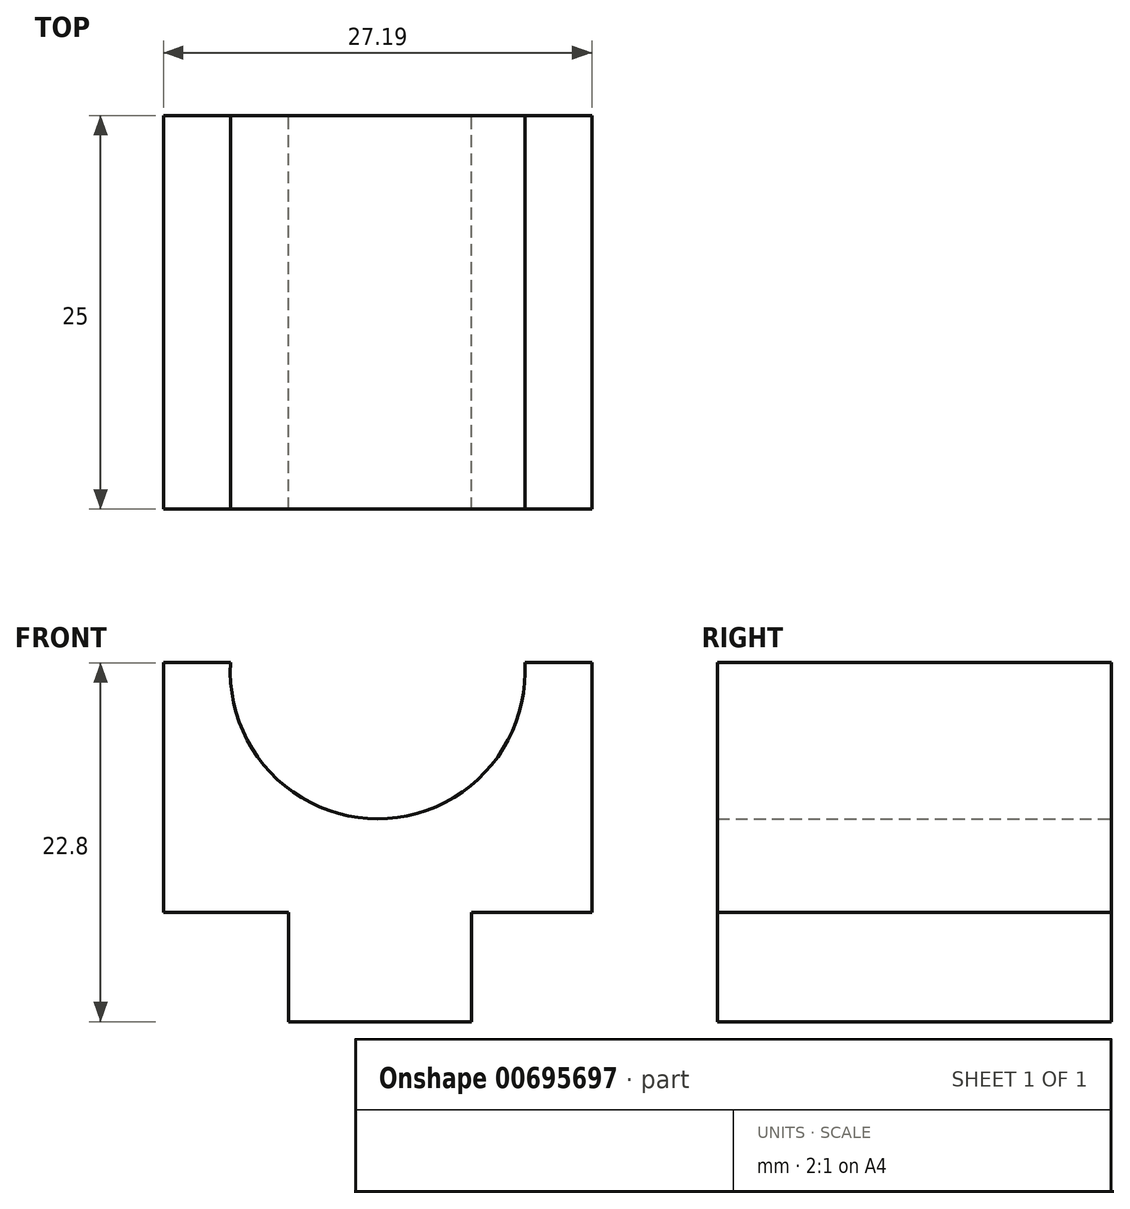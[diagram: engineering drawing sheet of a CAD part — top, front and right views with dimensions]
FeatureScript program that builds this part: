
annotation { "Feature Type Name" : "Feature", "Feature Type Description" : "" }
export const myFeature = defineFeature(function(context is Context, id is Id, definition is map)
    precondition{}
    {
        {
            var Q0;
            Q0=qCreatedBy(makeId("Front.planeOp"),FACE);
            var sketch = newSketch(context, id + "F0", { "sketchPlane" : qUnion([Q0])});
            skLineSegment(sketch, "E0", {"start": v(19.69, 0) * mm, "end": v(31.3, 0) * mm});
            skLineSegment(sketch, "E1", {"start": v(31.3, 0) * mm, "end": v(31.3, 6.94) * mm});
            skLineSegment(sketch, "E2", {"start": v(19.69, 0) * mm, "end": v(19.69, 6.94) * mm});
            skLineSegment(sketch, "E3", {"start": v(19.69, 6.94) * mm, "end": v(11.76, 6.94) * mm});
            skLineSegment(sketch, "E4", {"start": v(31.3, 6.94) * mm, "end": v(38.95, 6.94) * mm});
            skLineSegment(sketch, "E5", {"start": v(38.95, 6.94) * mm, "end": v(38.95, 22.8) * mm});
            skLineSegment(sketch, "E6", {"start": v(11.76, 6.94) * mm, "end": v(11.76, 22.8) * mm});
            skLineSegment(sketch, "E7", {"start": v(11.76, 22.8) * mm, "end": v(16, 22.8) * mm});
            skLineSegment(sketch, "E8", {"start": v(38.95, 22.8) * mm, "end": v(34.7, 22.8) * mm});
            skArc(sketch, "E9", {"start": v(16, 22.8) * mm, "mid": v(25.35, 12.89) * mm, "end": v(34.7, 22.8) * mm});
            skSolve(sketch);
        }
        {
            var Q0;
            Q0 = qSketchRegion(id + "F0", true);
            extrude(context, id + "F1", {"entities" : qUnion([Q0]), "depth" : 25 * mm, "offsetDistance" : 25 * mm});
        }
    });
